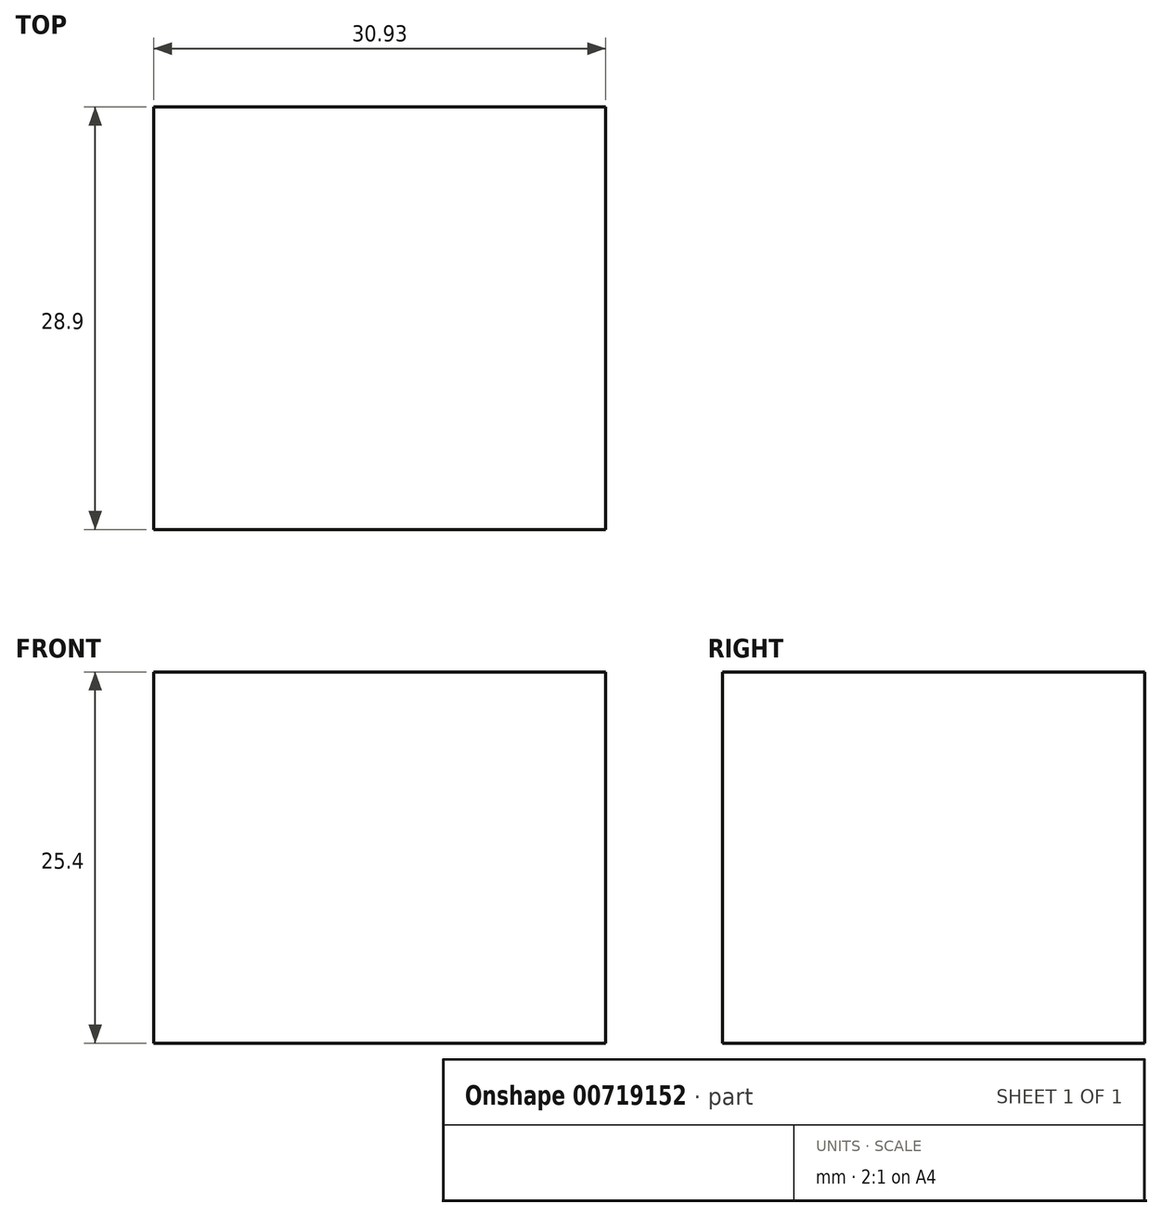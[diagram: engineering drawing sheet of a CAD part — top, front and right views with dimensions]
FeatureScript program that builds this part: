
annotation { "Feature Type Name" : "Feature", "Feature Type Description" : "" }
export const myFeature = defineFeature(function(context is Context, id is Id, definition is map)
    precondition{}
    {
        {
            var Q0;
            Q0=qCreatedBy(makeId("Top.planeOp"),FACE);
            var sketch = newSketch(context, id + "F0", { "sketchPlane" : qUnion([Q0])});
            skLineSegment(sketch, "E0", {"start": v(0, 0) * mm, "end": v(51.25, 0) * mm});
            skLineSegment(sketch, "E1", {"start": v(51.25, 0) * mm, "end": v(51.25, 28.9) * mm});
            skLineSegment(sketch, "E2", {"start": v(51.25, 28.9) * mm, "end": v(20.32, 28.9) * mm});
            skLineSegment(sketch, "E3", {"start": v(20.32, 28.9) * mm, "end": v(20.32, 0) * mm});
            skSolve(sketch);
        }
        {
            var Q0;
            {var subQ0=sQuery(id+"F0.wireOp",EDGE,"E1");Q0=makeQuery(id+"F0.imprint","IMPRINT",FACE,{"disambiguationData":[TD([[makeQuery(id+"F0.imprint","IMPRINT",EDGE,{"derivedFrom":subQ0}),1.0]])]});}
            extrude(context, id + "F1", {"entities" : qUnion([Q0]), "depth" : 25.4 * mm, "offsetDistance" : 25.4 * mm});
        }
    });
